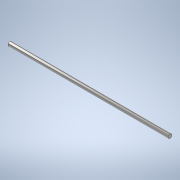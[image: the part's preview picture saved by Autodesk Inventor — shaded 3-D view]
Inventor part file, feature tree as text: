
AUTODESK INVENTOR PART (.ipt)
format: ipt  version: 2022 (Build 260153070, 153G)  size: 93,696 bytes
history: native  units: in
note: dims shown in document units (in); Inventor stores cm internally (conversion verified against a paired STEP export)
features: extrude x1, sketch x1
ambient origin geometry x8: Origin, YZ Plane, XZ Plane, XY Plane, X Axis, Y Axis, Z Axis, Center Point
bodies: Solid1 (feature_tree)
feature tree (2):
  extrude  "Extrusion1"  Depth=15.748in TaperAngle=0.0deg
  sketch  "Sketch1"  dims[d0=0.4in d1=15.748in d2=0.0in]
